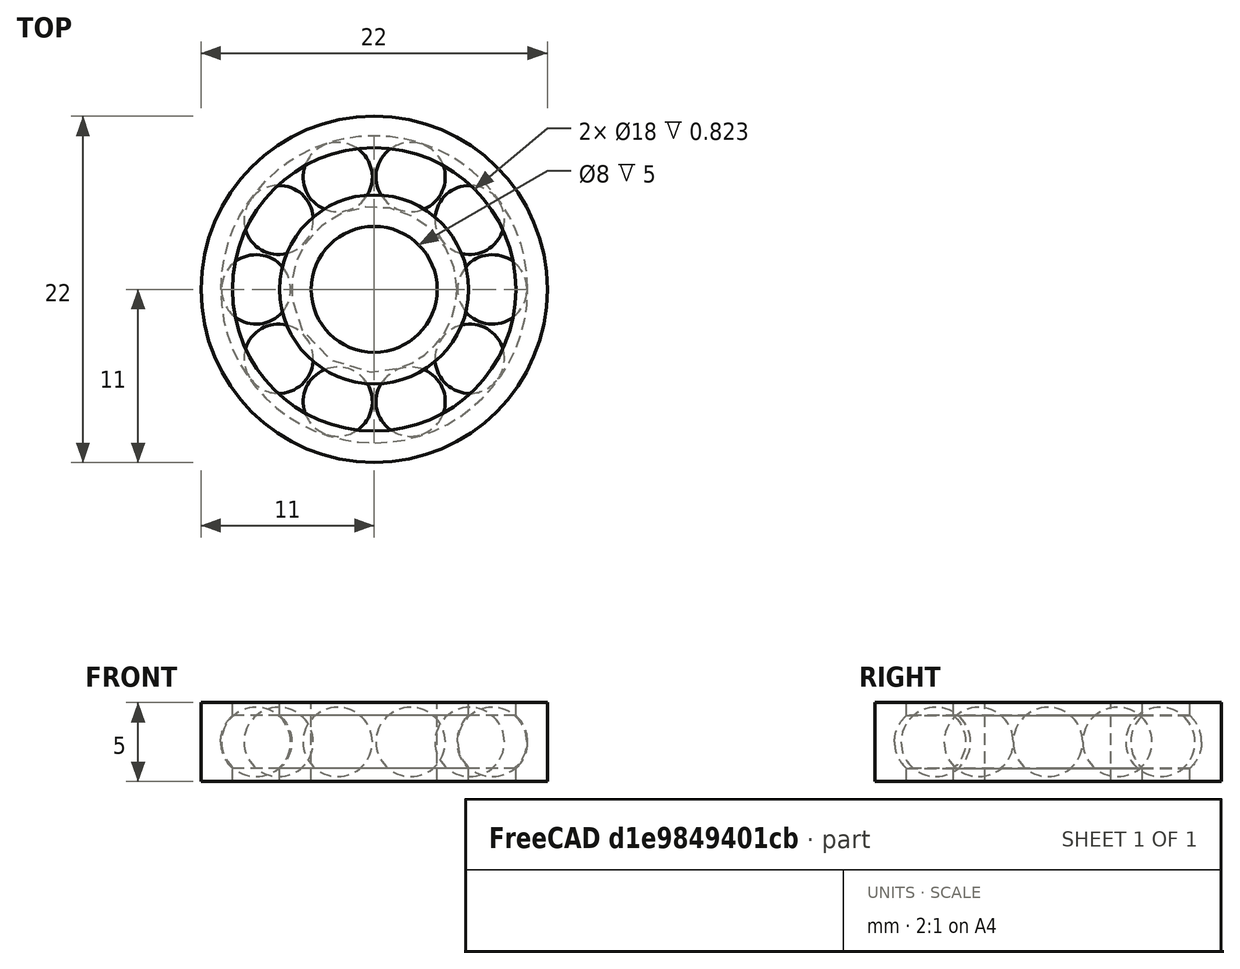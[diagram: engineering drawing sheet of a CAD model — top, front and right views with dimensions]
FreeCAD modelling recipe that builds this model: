
FCSTD DOCUMENT  (FreeCAD 0.15R4671 (Git))
Label: Ball Bearing
License: All rights reserved
LicenseURL: http://en.wikipedia.org/wiki/All_rights_reserved
objects: Part::Cylinder×4, Part::Cut×3, Part::MultiFuse×1, Part::Torus×1, Part::Sphere×1, Part::FeaturePython×1
note: 11 computed .brp shape members not serialized (recipe doc carries the construction recipe); baked Part::Feature solids carry a one-line shape summary decoded from their .brp

FEATURE [Part::Cylinder] Cylinder
  Angle = 360
  Height = 5
  Radius = 11
FEATURE [Part::Cylinder] Cylinder001
  Angle = 360
  Height = 10
  Placement = pos=(0,0,-2.5) rot=(0,0,1;0rad)
  Radius = 9
FEATURE [Part::Cut] Cut
  Base = -> Cylinder
  Tool = -> Cylinder001
FEATURE [Part::Cylinder] Cylinder002
  Angle = 360
  Height = 5
  Radius = 6
FEATURE [Part::Cylinder] Cylinder003
  Angle = 360
  Height = 10
  Placement = pos=(0,0,-2.5) rot=(0,0,1;0rad)
  Radius = 4
FEATURE [Part::Cut] Cut001
  Base = -> Cylinder002
  Tool = -> Cylinder003
FEATURE [Part::MultiFuse] Fusion
  Shapes = -> [Cut,Cut001]
FEATURE [Part::Torus] Torus
  Angle1 = -180
  Angle2 = 180
  Angle3 = 360
  Placement = pos=(0,0,2.5) rot=(0,0,1;0rad)
  Radius1 = 7.5
  Radius2 = 2.25
FEATURE [Part::Cut] Cut002
  Base = -> Fusion
  Tool = -> Torus
FEATURE [Part::Sphere] Sphere
  Angle1 = -90
  Angle2 = 90
  Angle3 = 360
  Placement = pos=(7.5,0,2.5) rot=(0,0,1;0rad)
  Radius = 2.2
FEATURE [Part::FeaturePython] Array  # Draft array (typed FeaturePython)
  Angle = 360
  ArrayType = 1
  Axis = (0,0,1)
  Base = -> Sphere
  Center = (0,0,0)
  Fuse = false
  IntervalAxis = (0,0,0)
  IntervalX = (1,0,0)
  IntervalY = (0,1,0)
  IntervalZ = (0,0,0)
  NumberPolar = 10
  NumberX = 2
  NumberY = 2
  NumberZ = 1
